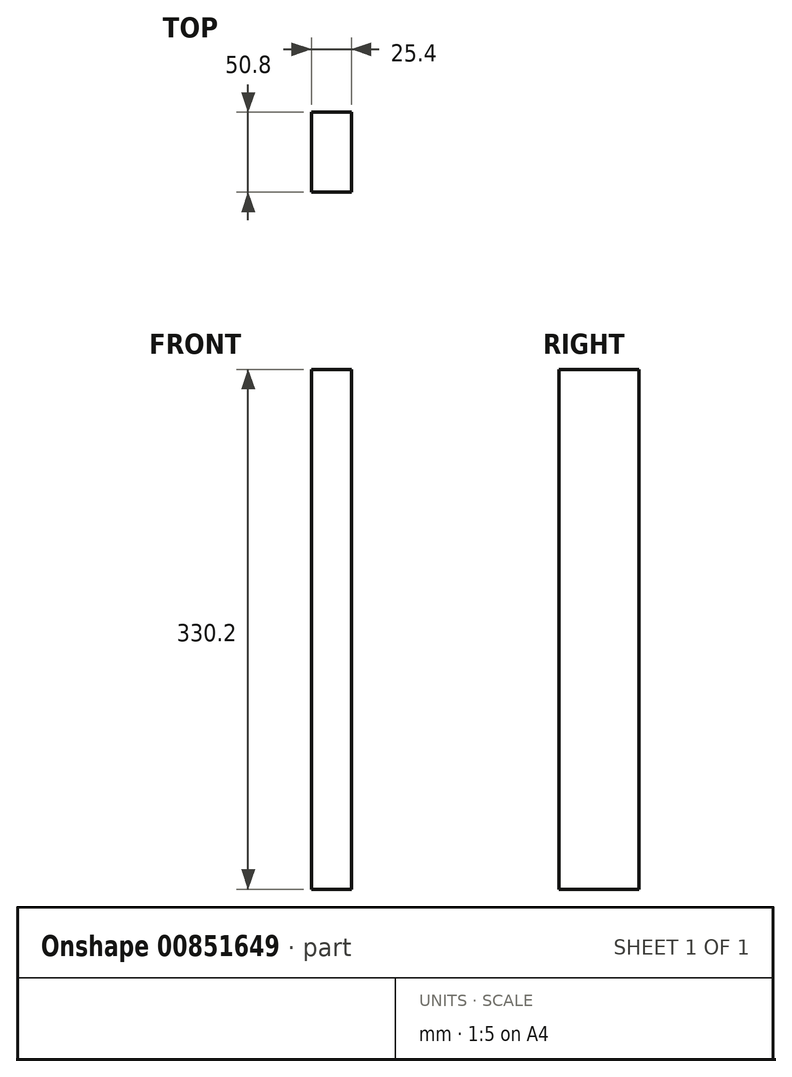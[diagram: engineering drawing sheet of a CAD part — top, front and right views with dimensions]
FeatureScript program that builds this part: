
annotation { "Feature Type Name" : "Feature", "Feature Type Description" : "" }
export const myFeature = defineFeature(function(context is Context, id is Id, definition is map)
    precondition{}
    {
        {
            var Q0;
            Q0=qCreatedBy(makeId("Front.planeOp"),FACE);
            var sketch = newSketch(context, id + "F0", { "sketchPlane" : qUnion([Q0])});
            skLineSegment(sketch, "E0", {"start": v(-26.77, 170.02) * mm, "end": v(-26.77, -160.18) * mm});
            skLineSegment(sketch, "E1", {"start": v(-26.77, 170.02) * mm, "end": v(-1.37, 170.02) * mm});
            skLineSegment(sketch, "E2", {"start": v(-1.37, 170.02) * mm, "end": v(-1.37, -160.18) * mm});
            skLineSegment(sketch, "E3", {"start": v(-1.37, -160.18) * mm, "end": v(-26.77, -160.18) * mm});
            skSolve(sketch);
        }
        {
            var Q0;
            Q0 = qSketchRegion(id + "F0", true);
            extrude(context, id + "F1", {"entities" : qUnion([Q0]), "depth" : 50.8 * mm, "offsetDistance" : 25.4 * mm});
        }
    });
